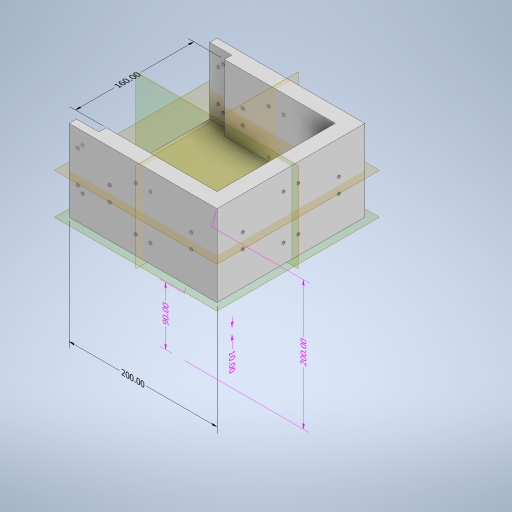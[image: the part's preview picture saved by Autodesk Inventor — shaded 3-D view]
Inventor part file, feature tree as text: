
AUTODESK INVENTOR PART (.ipt)
format: ipt  version: 2023 (Build 270158000, 158)  size: 442,880 bytes
history: native  units: mm
features: sketch x9, other x8, extrude x5, hole x4, plane x4, split x1
ambient origin geometry x8: Origin, YZ Plane, XZ Plane, XY Plane, X Axis, Y Axis, Z Axis, Center Point
bodies: Body1 (feature_tree)
feature tree (31):
  other  "Sólido1"
  other  "Anotaciones"
  extrude  "Extrusión1"  Depth=200.0mm
  hole  "Agujero1"  [1 undecoded]
  extrude  "Extrusión2"  Depth=15.0mm
  extrude  "Extrusión3"  Depth=20.0mm TaperAngle=0.0deg
  extrude  "Extrusión4"  Depth=200.0mm
  extrude  "Extrusión5"  Depth=20.0mm
  hole  "Agujero2"  [1 undecoded]
  plane  "Plano de trabajo1"
  split  "Dividir1"
  plane  "Plano de trabajo2"
  plane  "Plano de trabajo3"
  plane  "Plano de trabajo4"
  hole  "Agujero3"  [1 undecoded]
  hole  "Agujero4"  [1 undecoded]
  sketch  "Boceto2"  dims[d7=15.0mm d8=200.0mm]
  sketch  "Boceto3"  dims[d9=10.0mm d10=0.0mm]
  sketch  "Boceto4"  dims[d11=3.5mm d12=1.75mm d13=1.75mm d14=1.75mm d15=1.75mm d16=10.0mm d17=10.0mm d19=40.0mm]
  sketch  "Boceto5"  dims[d20=3.5mm d21=6.0mm d22=4.0mm d23=2.0mm d24=90.0deg d25=8.0mm d26=20.594885mm d27=15.0mm]
  sketch  "Boceto6"  dims[d28=20.0mm d29=80.0mm d30=0.0mm]
  sketch  "Boceto7"  dims[d31=57.0mm d32=200.0mm]
  sketch  "Boceto8"  dims[d33=110.0mm d34=0.0mm d36=20.0mm]
  sketch  "Boceto9"  dims[d37=20.0mm d38=20.0mm]
  sketch  "Boceto10"  dims[d39=90.0mm d40=0.0mm d43=30.0mm d44=0.0mm d45=3.5mm d46=1.75mm d47=1.75mm d48=1.75mm d49=1.75mm d50=10.0mm d51=10.0mm d52=15.0mm d53=10.0mm d54=10.0mm d55=15.0mm d56=3.5mm d57=6.0mm d58=4.0mm d59=2.0mm d60=90.0deg d61=8.0mm d62=20.594885mm d63=10.0mm d65=10.0mm d75=200.0mm d76=10.0mm d77=20.0mm d81=40.0mm d88=90.0deg d89=10.0mm d90=30.0mm d91=5.0mm d92=5.0mm d93=5.0mm d94=5.0mm d95=30.0mm d96=5.0mm d97=5.0mm d98=3.5mm d99=5.0mm d100=5.0mm d101=5.0mm d102=5.0mm d103=5.0mm d104=20.0mm d105=3.5mm d106=6.0mm d107=4.0mm d108=2.0mm d109=90.0deg d110=8.0mm d111=20.594885mm d112=10.0mm d113=30.0mm d114=5.0mm d115=5.0mm d116=5.0mm d117=5.0mm d118=5.0mm d119=5.0mm d120=3.5mm d121=5.0mm d122=5.0mm d123=5.0mm d124=5.0mm d125=5.0mm d126=30.0mm d127=30.0mm d128=3.5mm d129=6.0mm d130=4.0mm d131=2.0mm d132=90.0deg d133=8.0mm d134=20.594885mm d66=5.760865mm d67=7.72461mm d68=200.0mm d69=3.008686mm d70=2.422102mm d71=10.0mm d72=3.500509mm d73=2.402572mm d74=90.0mm d78=3.13122mm d79=6.269346mm d80=200.0mm d82=8.450127mm d83=0.968417mm d84=20.0mm d85=4.759975mm d86=4.646891mm d87=160.0mm]
  other  "Cota lineal 1"
  other  "Cota lineal 2"
  other  "Cota lineal 3"
  other  "Cota lineal 4"
  other  "Cota lineal 5"
  other  "Cota lineal 6"
note: 4 required parameter values undecoded (feature->parameter linkage not recoverable at this tier; creation-order binding heuristic only, values carry confidence <= 0.55)
